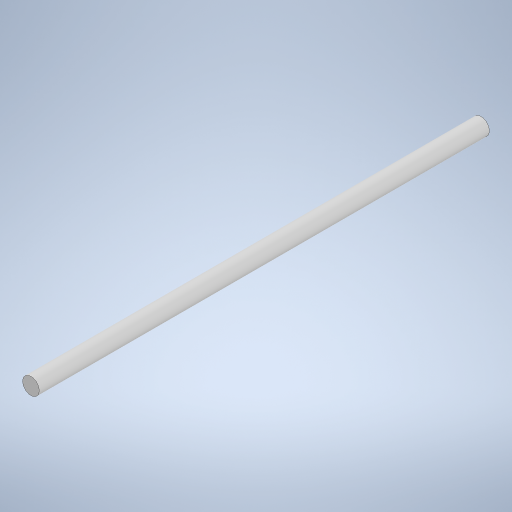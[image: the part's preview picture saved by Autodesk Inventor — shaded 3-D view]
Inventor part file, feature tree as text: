
AUTODESK INVENTOR PART (.ipt)
format: ipt  version: 2024 (Build 280153000, 153)  size: 233,984 bytes
history: native  units: mm
features: extrude x1, sketch x1
ambient origin geometry x8: Origin, YZ Plane, XZ Plane, XY Plane, X Axis, Y Axis, Z Axis, Center Point
bodies: Solid1 (feature_tree)
feature tree (2):
  extrude  "Extrusion1"  Depth=340.0mm TaperAngle=0.0deg
  sketch  "Sketch1"  dims[d0=12.7mm d1=340.0mm d2=0.0mm d3=0.5mm d4=0.872665mm]
